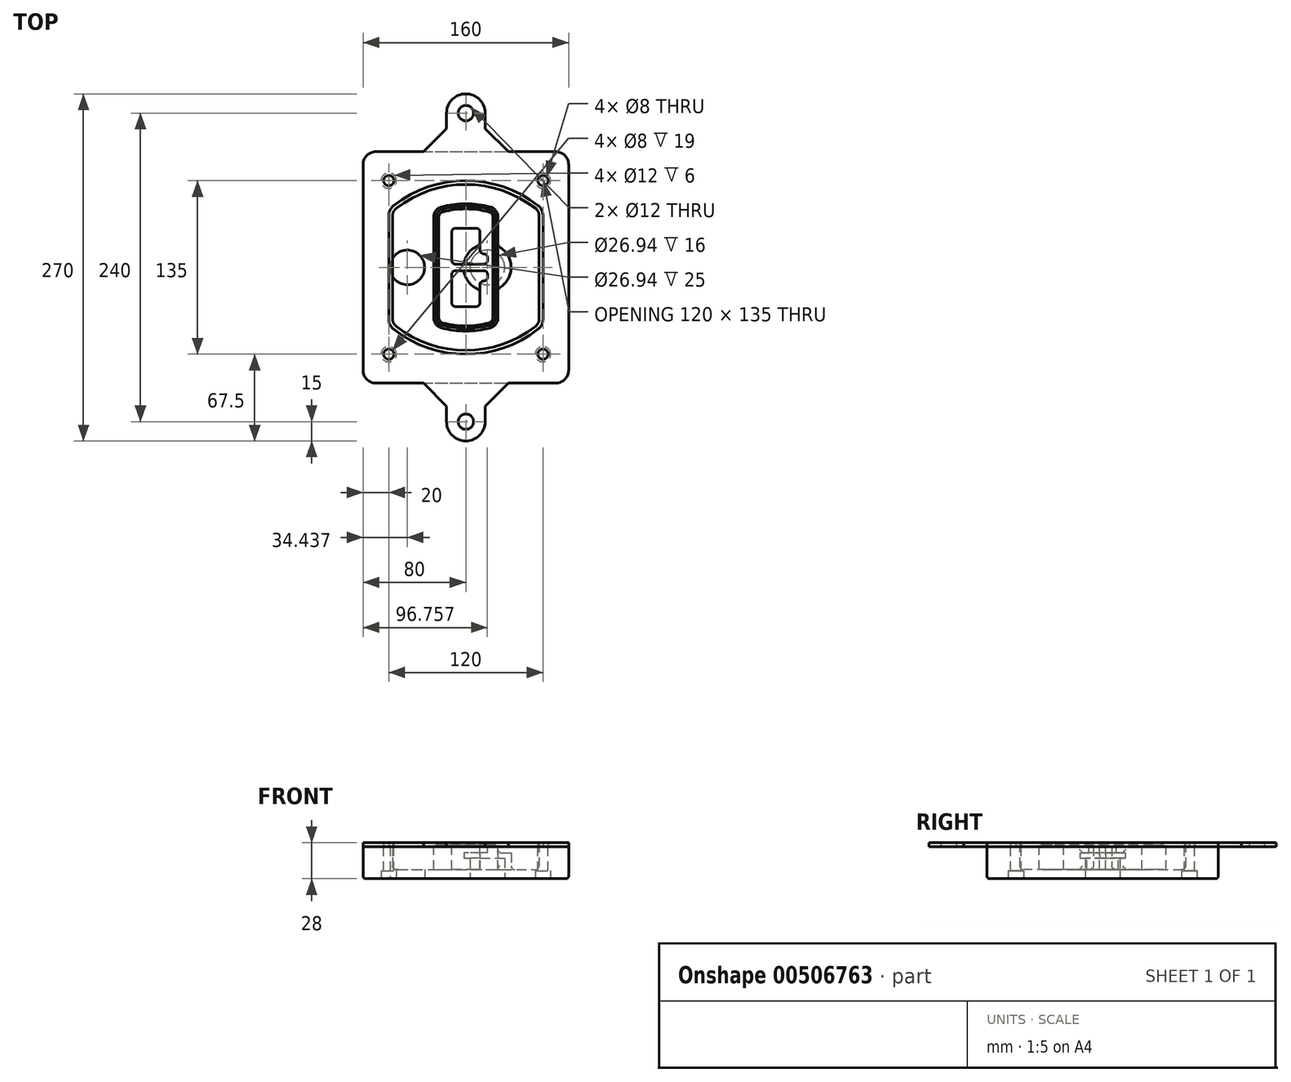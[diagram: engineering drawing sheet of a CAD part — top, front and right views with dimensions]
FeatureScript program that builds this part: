
annotation { "Feature Type Name" : "Feature", "Feature Type Description" : "" }
export const myFeature = defineFeature(function(context is Context, id is Id, definition is map)
    precondition{}
    {
        {
            var Q0;
            Q0=qCreatedBy(makeId("Top.planeOp"),FACE);
            var sketch = newSketch(context, id + "F0", { "sketchPlane" : qUnion([Q0])});
            skPoint(sketch, "E0.rect.middle", {"position": v(0, 0) * mm});
            skLineSegment(sketch, "E1.bottom", {"start": v(-70, -90) * mm, "end": v(70, -90) * mm});
            skLineSegment(sketch, "E1.top", {"start": v(-70, 90) * mm, "end": v(70, 90) * mm});
            skLineSegment(sketch, "E1.left", {"start": v(-80, -80) * mm, "end": v(-80, 80) * mm});
            skLineSegment(sketch, "E1.right", {"start": v(80, -80) * mm, "end": v(80, 80) * mm});
            skLineSegment(sketch, "E2", {"start": v(-80, 90) * mm, "end": v(80, -90) * mm, "construction": true});
            skLineSegment(sketch, "E3", {"start": v(80, 90) * mm, "end": v(-80, -90) * mm, "construction": true});
            skCircle(sketch, "E4", {"center": v(-60, 67.5) * mm, "radius": 4 * mm});
            skCircle(sketch, "E5", {"center": v(60, 67.5) * mm, "radius": 4 * mm});
            skCircle(sketch, "E6", {"center": v(60, -67.5) * mm, "radius": 4 * mm});
            skCircle(sketch, "E7", {"center": v(-60, -67.5) * mm, "radius": 4 * mm});
            skLineSegment(sketch, "E8", {"start": v(-60, 67.5) * mm, "end": v(60, 67.5) * mm, "construction": true});
            skLineSegment(sketch, "E9", {"start": v(60, 67.5) * mm, "end": v(60, -67.5) * mm, "construction": true});
            skLineSegment(sketch, "E10", {"start": v(60, -67.5) * mm, "end": v(-60, -67.5) * mm, "construction": true});
            skLineSegment(sketch, "E11", {"start": v(-60, -67.5) * mm, "end": v(-60, 67.5) * mm, "construction": true});
            skLineSegment(sketch, "E12", {"start": v(-60, 40.3) * mm, "end": v(-60, -40.3) * mm});
            skLineSegment(sketch, "E13", {"start": v(60, 40.3) * mm, "end": v(60, -40.3) * mm});
            skArc(sketch, "E14", {"start": v(56.15, 48.18) * mm, "mid": v(0, 67.5) * mm, "end": v(-56.15, 48.18) * mm});
            skArc(sketch, "E15", {"start": v(-56.15, -48.18) * mm, "mid": v(0, -67.5) * mm, "end": v(56.15, -48.18) * mm});
            skLineSegment(sketch, "E16", {"start": v(-60, 0) * mm, "end": v(60, 0) * mm, "construction": true});
            skPoint(sketch, "E17.visualSharp", {"position": v(-60, -45) * mm});
            skArc(sketch, "E17.filletArc", {"start": v(-60, -40.3) * mm, "mid": v(-58.99, -44.68) * mm, "end": v(-56.15, -48.18) * mm});
            skPoint(sketch, "E18.visualSharp", {"position": v(-60, 45) * mm});
            skArc(sketch, "E18.filletArc", {"start": v(-56.15, 48.18) * mm, "mid": v(-58.99, 44.68) * mm, "end": v(-60, 40.3) * mm});
            skPoint(sketch, "E19.visualSharp", {"position": v(60, 45) * mm});
            skArc(sketch, "E19.filletArc", {"start": v(60, 40.3) * mm, "mid": v(58.99, 44.68) * mm, "end": v(56.15, 48.18) * mm});
            skPoint(sketch, "E20.visualSharp", {"position": v(60, -45) * mm});
            skArc(sketch, "E20.filletArc", {"start": v(56.15, -48.18) * mm, "mid": v(58.99, -44.68) * mm, "end": v(60, -40.3) * mm});
            skPoint(sketch, "E21.visualSharp", {"position": v(-80, 90) * mm});
            skArc(sketch, "E21.filletArc", {"start": v(-70, 90) * mm, "mid": v(-77.07, 87.07) * mm, "end": v(-80, 80) * mm});
            skPoint(sketch, "E22.visualSharp", {"position": v(80, 90) * mm});
            skArc(sketch, "E22.filletArc", {"start": v(80, 80) * mm, "mid": v(77.07, 87.07) * mm, "end": v(70, 90) * mm});
            skPoint(sketch, "E23.visualSharp", {"position": v(80, -90) * mm});
            skArc(sketch, "E23.filletArc", {"start": v(70, -90) * mm, "mid": v(77.07, -87.07) * mm, "end": v(80, -80) * mm});
            skPoint(sketch, "E24.visualSharp", {"position": v(-80, -90) * mm});
            skArc(sketch, "E24.filletArc", {"start": v(-80, -80) * mm, "mid": v(-77.07, -87.07) * mm, "end": v(-70, -90) * mm});
            skArc(sketch, "E25.0", {"start": v(57, 40.3) * mm, "mid": v(56.3, 43.36) * mm, "end": v(54.3, 45.81) * mm});
            skLineSegment(sketch, "E25.1", {"start": v(57, 40.3) * mm, "end": v(57, -40.3) * mm});
            skArc(sketch, "E25.2", {"start": v(54.3, -45.81) * mm, "mid": v(56.3, -43.36) * mm, "end": v(57, -40.3) * mm});
            skArc(sketch, "E25.3", {"start": v(-54.3, -45.81) * mm, "mid": v(0, -64.5) * mm, "end": v(54.3, -45.81) * mm});
            skArc(sketch, "E25.4", {"start": v(-57, -40.3) * mm, "mid": v(-56.3, -43.36) * mm, "end": v(-54.3, -45.81) * mm});
            skArc(sketch, "E25.5", {"start": v(54.3, 45.81) * mm, "mid": v(0, 64.5) * mm, "end": v(-54.3, 45.81) * mm});
            skLineSegment(sketch, "E25.6", {"start": v(-57, 40.3) * mm, "end": v(-57, -40.3) * mm});
            skArc(sketch, "E25.7", {"start": v(-54.3, 45.81) * mm, "mid": v(-56.3, 43.36) * mm, "end": v(-57, 40.3) * mm});
            skArc(sketch, "E26.0", {"start": v(-58.62, 51.33) * mm, "mid": v(-62.58, 46.43) * mm, "end": v(-64, 40.3) * mm});
            skArc(sketch, "E26.1", {"start": v(58.62, 51.33) * mm, "mid": v(0, 71.5) * mm, "end": v(-58.62, 51.33) * mm});
            skArc(sketch, "E26.2", {"start": v(64, 40.3) * mm, "mid": v(62.58, 46.43) * mm, "end": v(58.62, 51.33) * mm});
            skLineSegment(sketch, "E26.3", {"start": v(64, 40.3) * mm, "end": v(64, -40.3) * mm});
            skArc(sketch, "E26.4", {"start": v(58.62, -51.33) * mm, "mid": v(62.58, -46.43) * mm, "end": v(64, -40.3) * mm});
            skLineSegment(sketch, "E26.5", {"start": v(-64, 40.3) * mm, "end": v(-64, -40.3) * mm});
            skArc(sketch, "E26.6", {"start": v(-58.62, -51.33) * mm, "mid": v(0, -71.5) * mm, "end": v(58.62, -51.33) * mm});
            skArc(sketch, "E26.7", {"start": v(-64, -40.3) * mm, "mid": v(-62.58, -46.43) * mm, "end": v(-58.62, -51.33) * mm});
            skSolve(sketch);
        }
        {
            var Q0;
            Q0=makeQuery(id+"F0.imprint","IMPRINT",FACE,{"disambiguationData":[TD([[makeQuery(id+"F0.imprint","IMPRINT",EDGE,{"derivedFrom":sQuery(id+"F0.wireOp",EDGE,"E1.bottom")}),1.0]])]});
            var Q1;
            Q1=makeQuery(id+"F0.imprint","IMPRINT",FACE,{"disambiguationData":[TD([[makeQuery(id+"F0.imprint","IMPRINT",EDGE,{"derivedFrom":sQuery(id+"F0.wireOp",EDGE,"E12")}),1.0]])]});
            var Q2;
            Q2=makeQuery(id+"F0.imprint","IMPRINT",FACE,{"disambiguationData":[TD([[makeQuery(id+"F0.imprint","IMPRINT",EDGE,{"derivedFrom":sQuery(id+"F0.wireOp",EDGE,"E25.0")}),1.0]])]});
            var Q3;
            Q3=makeQuery(id+"F0.imprint","IMPRINT",FACE,{"disambiguationData":[TD([[makeQuery(id+"F0.imprint","IMPRINT",EDGE,{"derivedFrom":sQuery(id+"F0.wireOp",EDGE,"E12")}),-1.0]])]});
            extrude(context, id + "F1", {"entities" : qUnion([Q0, Q1, Q2, Q3]), "oppositeDirection" : true, "depth" : 25 * mm});
        }
        {
            var Q0;
            Q0=makeQuery(id+"F0.imprint","IMPRINT",FACE,{"disambiguationData":[TD([[makeQuery(id+"F0.imprint","IMPRINT",EDGE,{"derivedFrom":sQuery(id+"F0.wireOp",EDGE,"E12")}),1.0]])]});
            extrude(context, id + "F2", {"entities" : qUnion([Q0]), "operationType" : NewBodyOperationType.ADD, "depth" : 3 * mm});
        }
        {
            var Q0;
            Q0=makeQuery(id+"F0.imprint","IMPRINT",FACE,{"disambiguationData":[TD([[makeQuery(id+"F0.imprint","IMPRINT",EDGE,{"derivedFrom":sQuery(id+"F0.wireOp",EDGE,"E25.0")}),1.0]])]});
            extrude(context, id + "F3", {"entities" : qUnion([Q0]), "operationType" : NewBodyOperationType.REMOVE, "oppositeDirection" : true, "depth" : 18 * mm});
        }
        {
            var Q0;
            Q0=makeQuery(id+"F2.opExtrude","CAP_FACE",FACE,{"disambiguationData":[OSD([sQuery(id+"F0.wireOp",EDGE,"E12"),sQuery(id+"F0.wireOp",EDGE,"E13"),sQuery(id+"F0.wireOp",EDGE,"E14"),sQuery(id+"F0.wireOp",EDGE,"E15"),sQuery(id+"F0.wireOp",EDGE,"E17.filletArc"),sQuery(id+"F0.wireOp",EDGE,"E18.filletArc"),sQuery(id+"F0.wireOp",EDGE,"E19.filletArc"),sQuery(id+"F0.wireOp",EDGE,"E20.filletArc"),sQuery(id+"F0.wireOp",EDGE,"E25.0"),sQuery(id+"F0.wireOp",EDGE,"E25.1"),sQuery(id+"F0.wireOp",EDGE,"E25.2"),sQuery(id+"F0.wireOp",EDGE,"E25.3"),sQuery(id+"F0.wireOp",EDGE,"E25.4"),sQuery(id+"F0.wireOp",EDGE,"E25.5"),sQuery(id+"F0.wireOp",EDGE,"E25.6"),sQuery(id+"F0.wireOp",EDGE,"E25.7")])],"isStart":false});
            var sketch = newSketch(context, id + "F4", { "sketchPlane" : qUnion([Q0])});
            skArc(sketch, "E27.0", {"start": v(-19.08, -46.97) * mm, "mid": v(0, -49.5) * mm, "end": v(19.08, -46.97) * mm});
            skArc(sketch, "E28.0", {"start": v(19.08, 46.97) * mm, "mid": v(0, 49.5) * mm, "end": v(-19.08, 46.97) * mm});
            skLineSegment(sketch, "E29", {"start": v(-25, 39.25) * mm, "end": v(-25, -39.25) * mm});
            skLineSegment(sketch, "E30", {"start": v(25, 39.25) * mm, "end": v(25, -39.25) * mm});
            skLineSegment(sketch, "E31", {"start": v(-25, 45.1) * mm, "end": v(25, 45.1) * mm, "construction": true});
            skLineSegment(sketch, "E32", {"start": v(-25, -45.1) * mm, "end": v(25, -45.1) * mm, "construction": true});
            skPoint(sketch, "E33.visualSharp", {"position": v(-25, 45.1) * mm});
            skArc(sketch, "E33.filletArc", {"start": v(-19.08, 46.97) * mm, "mid": v(-23.35, 44.11) * mm, "end": v(-25, 39.25) * mm});
            skPoint(sketch, "E34.visualSharp", {"position": v(25, 45.1) * mm});
            skArc(sketch, "E34.filletArc", {"start": v(25, 39.25) * mm, "mid": v(23.35, 44.11) * mm, "end": v(19.08, 46.97) * mm});
            skPoint(sketch, "E35.visualSharp", {"position": v(25, -45.1) * mm});
            skArc(sketch, "E35.filletArc", {"start": v(19.08, -46.97) * mm, "mid": v(23.35, -44.11) * mm, "end": v(25, -39.25) * mm});
            skPoint(sketch, "E36.visualSharp", {"position": v(-25, -45.1) * mm});
            skArc(sketch, "E36.filletArc", {"start": v(-25, -39.25) * mm, "mid": v(-23.35, -44.11) * mm, "end": v(-19.08, -46.97) * mm});
            skArc(sketch, "E37.0", {"start": v(54.3, 45.81) * mm, "mid": v(0, 64.5) * mm, "end": v(-54.3, 45.81) * mm});
            skArc(sketch, "E37.1", {"start": v(-54.3, 45.81) * mm, "mid": v(-56.3, 43.36) * mm, "end": v(-57, 40.3) * mm});
            skLineSegment(sketch, "E37.2", {"start": v(-57, 40.3) * mm, "end": v(-57, -40.3) * mm});
            skArc(sketch, "E37.3", {"start": v(-57, -40.3) * mm, "mid": v(-56.3, -43.36) * mm, "end": v(-54.3, -45.81) * mm});
            skArc(sketch, "E37.4", {"start": v(-54.3, -45.81) * mm, "mid": v(0, -64.5) * mm, "end": v(54.3, -45.81) * mm});
            skArc(sketch, "E37.5", {"start": v(54.3, -45.81) * mm, "mid": v(56.3, -43.36) * mm, "end": v(57, -40.3) * mm});
            skLineSegment(sketch, "E37.6", {"start": v(57, 40.3) * mm, "end": v(57, -40.3) * mm});
            skArc(sketch, "E37.7", {"start": v(57, 40.3) * mm, "mid": v(56.3, 43.36) * mm, "end": v(54.3, 45.81) * mm});
            skLineSegment(sketch, "E38.0", {"start": v(23, 39.25) * mm, "end": v(23, -39.25) * mm});
            skArc(sketch, "E38.1", {"start": v(18.56, -45.04) * mm, "mid": v(21.76, -42.9) * mm, "end": v(23, -39.25) * mm});
            skArc(sketch, "E38.2", {"start": v(-18.56, -45.04) * mm, "mid": v(0, -47.5) * mm, "end": v(18.56, -45.04) * mm});
            skArc(sketch, "E38.3", {"start": v(-23, -39.25) * mm, "mid": v(-21.76, -42.9) * mm, "end": v(-18.56, -45.04) * mm});
            skLineSegment(sketch, "E38.4", {"start": v(-23, 39.25) * mm, "end": v(-23, -39.25) * mm});
            skArc(sketch, "E38.5", {"start": v(23, 39.25) * mm, "mid": v(21.76, 42.9) * mm, "end": v(18.56, 45.04) * mm});
            skArc(sketch, "E38.6", {"start": v(-18.56, 45.04) * mm, "mid": v(-21.76, 42.9) * mm, "end": v(-23, 39.25) * mm});
            skArc(sketch, "E38.7", {"start": v(18.56, 45.04) * mm, "mid": v(0, 47.5) * mm, "end": v(-18.56, 45.04) * mm});
            skArc(sketch, "E39.0", {"start": v(21, 39.25) * mm, "mid": v(20.18, 41.68) * mm, "end": v(18.04, 43.1) * mm});
            skLineSegment(sketch, "E39.1", {"start": v(21, 39.25) * mm, "end": v(21, -39.25) * mm});
            skArc(sketch, "E39.2", {"start": v(18.04, -43.1) * mm, "mid": v(20.18, -41.68) * mm, "end": v(21, -39.25) * mm});
            skArc(sketch, "E39.3", {"start": v(-18.04, -43.1) * mm, "mid": v(0, -45.5) * mm, "end": v(18.04, -43.1) * mm});
            skArc(sketch, "E39.4", {"start": v(-21, -39.25) * mm, "mid": v(-20.18, -41.68) * mm, "end": v(-18.04, -43.1) * mm});
            skArc(sketch, "E39.5", {"start": v(18.04, 43.1) * mm, "mid": v(0, 45.5) * mm, "end": v(-18.04, 43.1) * mm});
            skLineSegment(sketch, "E39.6", {"start": v(-21, 39.25) * mm, "end": v(-21, -39.25) * mm});
            skArc(sketch, "E39.7", {"start": v(-18.04, 43.1) * mm, "mid": v(-20.18, 41.68) * mm, "end": v(-21, 39.25) * mm});
            skLineSegment(sketch, "E40", {"start": v(-25, 0) * mm, "end": v(25, 0) * mm, "construction": true});
            skLineSegment(sketch, "E41", {"start": v(-11, 5.5) * mm, "end": v(-11, 27.5) * mm});
            skLineSegment(sketch, "E42", {"start": v(-8, 30.5) * mm, "end": v(8, 30.5) * mm});
            skLineSegment(sketch, "E43", {"start": v(11, 27.5) * mm, "end": v(11, 13.5) * mm});
            skLineSegment(sketch, "E44", {"start": v(14, 10.5) * mm, "end": v(14, 10.5) * mm});
            skLineSegment(sketch, "E45", {"start": v(17, 7.5) * mm, "end": v(17, 5.5) * mm});
            skLineSegment(sketch, "E46", {"start": v(14, 2.5) * mm, "end": v(-8, 2.5) * mm});
            skPoint(sketch, "E47.visualSharp", {"position": v(-11, 30.5) * mm});
            skArc(sketch, "E47.filletArc", {"start": v(-8, 30.5) * mm, "mid": v(-10.12, 29.62) * mm, "end": v(-11, 27.5) * mm});
            skPoint(sketch, "E48.visualSharp", {"position": v(11, 30.5) * mm});
            skArc(sketch, "E48.filletArc", {"start": v(11, 27.5) * mm, "mid": v(10.12, 29.62) * mm, "end": v(8, 30.5) * mm});
            skPoint(sketch, "E49.visualSharp", {"position": v(11, 10.5) * mm});
            skArc(sketch, "E49.filletArc", {"start": v(11, 13.5) * mm, "mid": v(11.88, 11.38) * mm, "end": v(14, 10.5) * mm});
            skPoint(sketch, "E50.visualSharp", {"position": v(17, 10.5) * mm});
            skArc(sketch, "E50.filletArc", {"start": v(17, 7.5) * mm, "mid": v(16.12, 9.62) * mm, "end": v(14, 10.5) * mm});
            skPoint(sketch, "E51.visualSharp", {"position": v(17, 2.5) * mm});
            skArc(sketch, "E51.filletArc", {"start": v(14, 2.5) * mm, "mid": v(16.12, 3.38) * mm, "end": v(17, 5.5) * mm});
            skPoint(sketch, "E52.visualSharp", {"position": v(-11, 2.5) * mm});
            skArc(sketch, "E52.filletArc", {"start": v(-11, 5.5) * mm, "mid": v(-10.12, 3.38) * mm, "end": v(-8, 2.5) * mm});
            skLineSegment(sketch, "E53.0.MirrorCS", {"start": v(14, -2.5) * mm, "end": v(-8, -2.5) * mm});
            skArc(sketch, "E54.0.MirrorCS", {"start": v(-11, -5.5) * mm, "mid": v(-10.12, -3.38) * mm, "end": v(-8, -2.5) * mm});
            skLineSegment(sketch, "E55.0.MirrorCS", {"start": v(-11, -5.5) * mm, "end": v(-11, -27.5) * mm});
            skArc(sketch, "E56.0.MirrorCS", {"start": v(-8, -30.5) * mm, "mid": v(-10.12, -29.62) * mm, "end": v(-11, -27.5) * mm});
            skLineSegment(sketch, "E57.0.MirrorCS", {"start": v(-8, -30.5) * mm, "end": v(8, -30.5) * mm});
            skArc(sketch, "E58.0.MirrorCS", {"start": v(11, -27.5) * mm, "mid": v(10.12, -29.62) * mm, "end": v(8, -30.5) * mm});
            skLineSegment(sketch, "E59.0.MirrorCS", {"start": v(11, -27.5) * mm, "end": v(11, -13.5) * mm});
            skArc(sketch, "E60.0.MirrorCS", {"start": v(11, -13.5) * mm, "mid": v(11.88, -11.38) * mm, "end": v(14, -10.5) * mm});
            skArc(sketch, "E61.0.MirrorCS", {"start": v(17, -7.5) * mm, "mid": v(16.12, -9.62) * mm, "end": v(14, -10.5) * mm});
            skLineSegment(sketch, "E62.0.MirrorCS", {"start": v(17, -7.5) * mm, "end": v(17, -5.5) * mm});
            skArc(sketch, "E63.0.MirrorCS", {"start": v(14, -2.5) * mm, "mid": v(16.12, -3.38) * mm, "end": v(17, -5.5) * mm});
            skSolve(sketch);
        }
        {
            var Q0;
            Q0=makeQuery(id+"F4.imprint","IMPRINT",FACE,{"disambiguationData":[TD([[makeQuery(id+"F4.imprint","IMPRINT",EDGE,{"derivedFrom":sQuery(id+"F4.wireOp",EDGE,"E27.0")}),1.0]])]});
            var Q1;
            Q1=makeQuery(id+"F4.imprint","IMPRINT",FACE,{"disambiguationData":[TD([[makeQuery(id+"F4.imprint","IMPRINT",EDGE,{"derivedFrom":sQuery(id+"F4.wireOp",EDGE,"E38.0")}),-1.0]])]});
            var Q2;
            Q2=makeQuery(id+"F4.imprint","IMPRINT",FACE,{"disambiguationData":[TD([[makeQuery(id+"F4.imprint","IMPRINT",EDGE,{"derivedFrom":sQuery(id+"F4.wireOp",EDGE,"E39.0")}),1.0]])]});
            extrude(context, id + "F5", {"entities" : qUnion([Q0, Q1, Q2]), "operationType" : NewBodyOperationType.ADD, "endBound" : BoundingType.UP_TO_NEXT, "oppositeDirection" : true, "depth" : 25 * mm});
        }
        {
            var Q0;
            Q0=makeQuery(id+"F4.imprint","IMPRINT",FACE,{"disambiguationData":[TD([[makeQuery(id+"F4.imprint","IMPRINT",EDGE,{"derivedFrom":sQuery(id+"F4.wireOp",EDGE,"E38.0")}),-1.0]])]});
            extrude(context, id + "F6", {"entities" : qUnion([Q0]), "operationType" : NewBodyOperationType.REMOVE, "oppositeDirection" : true, "depth" : 2 * mm});
        }
        {
            var Q0;
            Q0=makeQuery(id+"F1.opExtrude","CAP_FACE",FACE,{"disambiguationData":[OSD([sQuery(id+"F0.wireOp",EDGE,"E1.bottom"),sQuery(id+"F0.wireOp",EDGE,"E1.top"),sQuery(id+"F0.wireOp",EDGE,"E1.left"),sQuery(id+"F0.wireOp",EDGE,"E1.right"),sQuery(id+"F0.wireOp",EDGE,"E4"),sQuery(id+"F0.wireOp",EDGE,"E5"),sQuery(id+"F0.wireOp",EDGE,"E6"),sQuery(id+"F0.wireOp",EDGE,"E7"),sQuery(id+"F0.wireOp",EDGE,"E21.filletArc"),sQuery(id+"F0.wireOp",EDGE,"E22.filletArc"),sQuery(id+"F0.wireOp",EDGE,"E23.filletArc"),sQuery(id+"F0.wireOp",EDGE,"E24.filletArc")])],"isStart":false});
            var sketch = newSketch(context, id + "F7", { "sketchPlane" : qUnion([Q0])});
            skCircle(sketch, "E64", {"center": v(16.76, 0) * mm, "radius": 13.47 * mm});
            skCircle(sketch, "E65", {"center": v(-45.56, 0) * mm, "radius": 13.47 * mm});
            skLineSegment(sketch, "E66", {"start": v(80, 0) * mm, "end": v(-80, 0) * mm});
            skCircle(sketch, "E67", {"center": v(16.76, 0) * mm, "radius": 18.47 * mm});
            skCircle(sketch, "E68", {"center": v(60, -67.5) * mm, "radius": 6 * mm});
            skCircle(sketch, "E69", {"center": v(-60, -67.5) * mm, "radius": 6 * mm});
            skCircle(sketch, "E70", {"center": v(-60, 67.5) * mm, "radius": 6 * mm});
            skCircle(sketch, "E71", {"center": v(60, 67.5) * mm, "radius": 6 * mm});
            skSolve(sketch);
        }
        {
            var Q0;
            {var subQ1=sQuery(id+"F7.wireOp",EDGE,"E66");var subQ4=sQuery(id+"F7.wireOp",EDGE,"E64");var subQ6=makeQuery(id+"F7.imprint","INTERSECT",VERTEX,{"disambiguationData":[OD(0.0)],"derivedFrom":[subQ4,subQ1]});Q0=makeQuery(id+"F7.imprint","IMPRINT",FACE,{"disambiguationData":[TD([[makeQuery(id+"F7.imprint","IMPRINT",EDGE,{"disambiguationData":[TD([[subQ6,-1.0]])],"derivedFrom":subQ4}),-1.0]])]});}
            var Q1;
            {var subQ0=sQuery(id+"F7.wireOp",EDGE,"E66");var subQ1=sQuery(id+"F7.wireOp",EDGE,"E64");var subQ3=makeQuery(id+"F7.imprint","INTERSECT",VERTEX,{"disambiguationData":[OD(0.0)],"derivedFrom":[subQ1,subQ0]});Q1=makeQuery(id+"F7.imprint","IMPRINT",FACE,{"disambiguationData":[TD([[makeQuery(id+"F7.imprint","IMPRINT",EDGE,{"disambiguationData":[TD([[subQ3,-1.0]])],"derivedFrom":subQ1}),1.0]])]});}
            var Q2;
            {var subQ0=sQuery(id+"F7.wireOp",EDGE,"E66");var subQ1=sQuery(id+"F7.wireOp",EDGE,"E64");var subQ3=makeQuery(id+"F7.imprint","INTERSECT",VERTEX,{"disambiguationData":[OD(0.0)],"derivedFrom":[subQ1,subQ0]});Q2=makeQuery(id+"F7.imprint","IMPRINT",FACE,{"disambiguationData":[TD([[makeQuery(id+"F7.imprint","IMPRINT",EDGE,{"disambiguationData":[TD([[subQ3,1.0]])],"derivedFrom":subQ1}),1.0]])]});}
            var Q3;
            {var subQ1=sQuery(id+"F7.wireOp",EDGE,"E66");var subQ4=sQuery(id+"F7.wireOp",EDGE,"E64");var subQ6=makeQuery(id+"F7.imprint","INTERSECT",VERTEX,{"disambiguationData":[OD(0.0)],"derivedFrom":[subQ4,subQ1]});Q3=makeQuery(id+"F7.imprint","IMPRINT",FACE,{"disambiguationData":[TD([[makeQuery(id+"F7.imprint","IMPRINT",EDGE,{"disambiguationData":[TD([[subQ6,1.0]])],"derivedFrom":subQ4}),-1.0]])]});}
            extrude(context, id + "F8", {"entities" : qUnion([Q0, Q1, Q2, Q3]), "operationType" : NewBodyOperationType.ADD, "oppositeDirection" : true, "depth" : 20 * mm});
        }
        {
            var Q0;
            {var subQ0=sQuery(id+"F7.wireOp",EDGE,"E66");var subQ1=sQuery(id+"F7.wireOp",EDGE,"E64");var subQ3=makeQuery(id+"F7.imprint","INTERSECT",VERTEX,{"disambiguationData":[OD(0.0)],"derivedFrom":[subQ1,subQ0]});Q0=makeQuery(id+"F7.imprint","IMPRINT",FACE,{"disambiguationData":[TD([[makeQuery(id+"F7.imprint","IMPRINT",EDGE,{"disambiguationData":[TD([[subQ3,-1.0]])],"derivedFrom":subQ1}),1.0]])]});}
            var Q1;
            {var subQ0=sQuery(id+"F7.wireOp",EDGE,"E66");var subQ1=sQuery(id+"F7.wireOp",EDGE,"E64");var subQ3=makeQuery(id+"F7.imprint","INTERSECT",VERTEX,{"disambiguationData":[OD(0.0)],"derivedFrom":[subQ1,subQ0]});Q1=makeQuery(id+"F7.imprint","IMPRINT",FACE,{"disambiguationData":[TD([[makeQuery(id+"F7.imprint","IMPRINT",EDGE,{"disambiguationData":[TD([[subQ3,1.0]])],"derivedFrom":subQ1}),1.0]])]});}
            extrude(context, id + "F9", {"entities" : qUnion([Q0, Q1]), "operationType" : NewBodyOperationType.REMOVE, "oppositeDirection" : true, "depth" : 16 * mm});
        }
        {
            var Q0;
            {var subQ0=sQuery(id+"F7.wireOp",EDGE,"E66");var subQ1=sQuery(id+"F7.wireOp",EDGE,"E65");var subQ3=makeQuery(id+"F7.imprint","INTERSECT",VERTEX,{"disambiguationData":[OD(0.0)],"derivedFrom":[subQ1,subQ0]});Q0=makeQuery(id+"F7.imprint","IMPRINT",FACE,{"disambiguationData":[TD([[makeQuery(id+"F7.imprint","IMPRINT",EDGE,{"disambiguationData":[TD([[subQ3,-1.0]])],"derivedFrom":subQ1}),1.0]])]});}
            var Q1;
            {var subQ0=sQuery(id+"F7.wireOp",EDGE,"E66");var subQ1=sQuery(id+"F7.wireOp",EDGE,"E65");var subQ3=makeQuery(id+"F7.imprint","INTERSECT",VERTEX,{"disambiguationData":[OD(0.0)],"derivedFrom":[subQ1,subQ0]});Q1=makeQuery(id+"F7.imprint","IMPRINT",FACE,{"disambiguationData":[TD([[makeQuery(id+"F7.imprint","IMPRINT",EDGE,{"disambiguationData":[TD([[subQ3,1.0]])],"derivedFrom":subQ1}),1.0]])]});}
            extrude(context, id + "F10", {"entities" : qUnion([Q0, Q1]), "operationType" : NewBodyOperationType.REMOVE, "oppositeDirection" : true, "depth" : 25 * mm});
        }
        {
            var Q0;
            Q0=makeQuery(id+"F7.imprint","IMPRINT",FACE,{"disambiguationData":[TD([[makeQuery(id+"F7.imprint","IMPRINT",EDGE,{"derivedFrom":sQuery(id+"F7.wireOp",EDGE,"E68")}),1.0]])]});
            var Q1;
            Q1=makeQuery(id+"F7.imprint","IMPRINT",FACE,{"disambiguationData":[TD([[makeQuery(id+"F7.imprint","IMPRINT",EDGE,{"derivedFrom":makeQuery(id+"F1.opExtrude","CAP_EDGE",EDGE,{"disambiguationData":[OSD([sQuery(id+"F0.wireOp",EDGE,"E5")])],"isStart":false})}),-1.0]])]});
            var Q2;
            Q2=makeQuery(id+"F7.imprint","IMPRINT",FACE,{"disambiguationData":[TD([[makeQuery(id+"F7.imprint","IMPRINT",EDGE,{"derivedFrom":sQuery(id+"F7.wireOp",EDGE,"E69")}),1.0]])]});
            var Q3;
            Q3=makeQuery(id+"F7.imprint","IMPRINT",FACE,{"disambiguationData":[TD([[makeQuery(id+"F7.imprint","IMPRINT",EDGE,{"derivedFrom":makeQuery(id+"F1.opExtrude","CAP_EDGE",EDGE,{"disambiguationData":[OSD([sQuery(id+"F0.wireOp",EDGE,"E4")])],"isStart":false})}),-1.0]])]});
            var Q4;
            Q4=makeQuery(id+"F7.imprint","IMPRINT",FACE,{"disambiguationData":[TD([[makeQuery(id+"F7.imprint","IMPRINT",EDGE,{"derivedFrom":sQuery(id+"F7.wireOp",EDGE,"E70")}),1.0]])]});
            var Q5;
            Q5=makeQuery(id+"F7.imprint","IMPRINT",FACE,{"disambiguationData":[TD([[makeQuery(id+"F7.imprint","IMPRINT",EDGE,{"derivedFrom":makeQuery(id+"F1.opExtrude","CAP_EDGE",EDGE,{"disambiguationData":[OSD([sQuery(id+"F0.wireOp",EDGE,"E7")])],"isStart":false})}),-1.0]])]});
            var Q6;
            Q6=makeQuery(id+"F7.imprint","IMPRINT",FACE,{"disambiguationData":[TD([[makeQuery(id+"F7.imprint","IMPRINT",EDGE,{"derivedFrom":sQuery(id+"F7.wireOp",EDGE,"E71")}),1.0]])]});
            var Q7;
            Q7=makeQuery(id+"F7.imprint","IMPRINT",FACE,{"disambiguationData":[TD([[makeQuery(id+"F7.imprint","IMPRINT",EDGE,{"derivedFrom":makeQuery(id+"F1.opExtrude","CAP_EDGE",EDGE,{"disambiguationData":[OSD([sQuery(id+"F0.wireOp",EDGE,"E6")])],"isStart":false})}),-1.0]])]});
            extrude(context, id + "F11", {"entities" : qUnion([Q0, Q1, Q2, Q3, Q4, Q5, Q6, Q7]), "operationType" : NewBodyOperationType.REMOVE, "oppositeDirection" : true, "depth" : 6 * mm});
        }
        {
            var Q0;
            Q0=makeQuery(id+"F9.boolean.opBoolean","COPY",FACE,{"derivedFrom":makeQuery(id+"F9.opExtrude","CAP_FACE",FACE,{"disambiguationData":[OSD([sQuery(id+"F7.wireOp",EDGE,"E64")])],"isStart":false})});
            var sketch = newSketch(context, id + "F12", { "sketchPlane" : qUnion([Q0])});
            skArc(sketch, "E72.0", {"start": v(11, 17.55) * mm, "mid": v(2.57, 11.82) * mm, "end": v(-1.54, 2.5) * mm});
            skArc(sketch, "E72.1", {"start": v(-1.54, -2.5) * mm, "mid": v(2.57, -11.82) * mm, "end": v(11, -17.55) * mm});
            skLineSegment(sketch, "E73", {"start": v(-1.54, -2.5) * mm, "end": v(14, -2.5) * mm});
            skLineSegment(sketch, "E74.0", {"start": v(14, 2.5) * mm, "end": v(-1.54, 2.5) * mm});
            skArc(sketch, "E74.1", {"start": v(14, 2.5) * mm, "mid": v(16.12, 3.38) * mm, "end": v(17, 5.5) * mm});
            skLineSegment(sketch, "E74.2", {"start": v(17, 7.5) * mm, "end": v(17, 5.5) * mm});
            skArc(sketch, "E74.3", {"start": v(17, 7.5) * mm, "mid": v(16.12, 9.62) * mm, "end": v(14, 10.5) * mm});
            skArc(sketch, "E74.4", {"start": v(11, 13.5) * mm, "mid": v(11.88, 11.38) * mm, "end": v(14, 10.5) * mm});
            skLineSegment(sketch, "E74.5", {"start": v(11, 17.55) * mm, "end": v(11, 13.5) * mm});
            skLineSegment(sketch, "E74.7", {"start": v(14, -2.5) * mm, "end": v(-1.54, -2.5) * mm});
            skArc(sketch, "E74.8", {"start": v(14, -2.5) * mm, "mid": v(16.12, -3.38) * mm, "end": v(17, -5.5) * mm});
            skLineSegment(sketch, "E74.9", {"start": v(17, -7.5) * mm, "end": v(17, -5.5) * mm});
            skArc(sketch, "E74.10", {"start": v(17, -7.5) * mm, "mid": v(16.12, -9.62) * mm, "end": v(14, -10.5) * mm});
            skArc(sketch, "E74.11", {"start": v(11, -13.5) * mm, "mid": v(11.88, -11.38) * mm, "end": v(14, -10.5) * mm});
            skLineSegment(sketch, "E74.12", {"start": v(11, -17.55) * mm, "end": v(11, -13.5) * mm});
            skPoint(sketch, "E75.orphan", {"position": v(11, -27.5) * mm});
            skPoint(sketch, "E76.orphan", {"position": v(-8, -2.5) * mm});
            skPoint(sketch, "E77.orphan", {"position": v(-8, 2.5) * mm});
            skPoint(sketch, "E78.orphan", {"position": v(11, 27.5) * mm});
            skSolve(sketch);
        }
        {
            var Q0;
            {var subQ7=sQuery(id+"F12.wireOp",EDGE,"E72.0");var subQ14=sQuery(id+"F12.wireOp",EDGE,"E72.1");var subQ16=sQuery(id+"F12.wireOp",EDGE,"E74.1");var subQ18=sQuery(id+"F12.wireOp",EDGE,"E74.8");Q0=qUnion([makeQuery(id+"F12.imprint","IMPRINT",FACE,{"disambiguationData":[TD([[makeQuery(id+"F12.imprint","IMPRINT",EDGE,{"derivedFrom":subQ7}),1.0]])]}),makeQuery(id+"F12.imprint","IMPRINT",FACE,{"disambiguationData":[TD([[makeQuery(id+"F12.imprint","IMPRINT",EDGE,{"derivedFrom":subQ14}),1.0]])]}),makeQuery(id+"F12.imprint","IMPRINT",FACE,{"disambiguationData":[TD([[makeQuery(id+"F12.imprint","IMPRINT",EDGE,{"derivedFrom":subQ16}),1.0]])]}),makeQuery(id+"F12.imprint","IMPRINT",FACE,{"disambiguationData":[TD([[makeQuery(id+"F12.imprint","IMPRINT",EDGE,{"derivedFrom":subQ18}),-1.0]])]})]);}
            var Q1;
            Q1=makeQuery(id+"F5.boolean.opBoolean","SPLIT",FACE,{"disambiguationData":[TD([makeQuery(id+"F5.opExtrude","SWEPT_FACE",FACE,{"disambiguationData":[OSD([sQuery(id+"F4.wireOp",EDGE,"E41")])]})])],"derivedFrom":makeQuery(id+"F3.boolean.opBoolean","COPY",FACE,{"derivedFrom":makeQuery(id+"F3.opExtrude","CAP_FACE",FACE,{"disambiguationData":[OSD([sQuery(id+"F0.wireOp",EDGE,"E25.0"),sQuery(id+"F0.wireOp",EDGE,"E25.1"),sQuery(id+"F0.wireOp",EDGE,"E25.2"),sQuery(id+"F0.wireOp",EDGE,"E25.3"),sQuery(id+"F0.wireOp",EDGE,"E25.4"),sQuery(id+"F0.wireOp",EDGE,"E25.5"),sQuery(id+"F0.wireOp",EDGE,"E25.6"),sQuery(id+"F0.wireOp",EDGE,"E25.7")])],"isStart":false})})});
            extrude(context, id + "F13", {"entities" : qUnion([Q0]), "operationType" : NewBodyOperationType.REMOVE, "endBound" : BoundingType.UP_TO_SURFACE, "endBoundEntityFace" : qUnion([Q1]), "depth" : 25 * mm});
        }
        {
            var Q0;
            Q0=makeQuery(id+"F3.boolean.opBoolean","COPY",EDGE,{"derivedFrom":makeQuery(id+"F3.opExtrude","CAP_EDGE",EDGE,{"disambiguationData":[OSD([sQuery(id+"F0.wireOp",EDGE,"E25.6")])],"isStart":false})});
            var Q1;
            Q1=makeQuery(id+"F8.boolean.opBoolean","INTERSECT",EDGE,{"derivedFrom":[makeQuery(id+"F5.opExtrude","SWEPT_FACE",FACE,{"disambiguationData":[OSD([sQuery(id+"F4.wireOp",EDGE,"E30")])]}),makeQuery(id+"F8.opExtrude","CAP_FACE",FACE,{"disambiguationData":[OSD([sQuery(id+"F7.wireOp",EDGE,"E67")])],"isStart":false})]});
            var Q2;
            Q2=makeQuery(id+"F8.boolean.opBoolean","INTERSECT",EDGE,{"disambiguationData":[OD(1.0)],"derivedFrom":[makeQuery(id+"F5.opExtrude","SWEPT_FACE",FACE,{"disambiguationData":[OSD([sQuery(id+"F4.wireOp",EDGE,"E30")])]}),makeQuery(id+"F8.opExtrude","SWEPT_FACE",FACE,{"disambiguationData":[OSD([sQuery(id+"F7.wireOp",EDGE,"E67")])]})]});
            var Q3;
            {var subQ0=makeQuery(id+"F3.boolean.opBoolean","COPY",FACE,{"derivedFrom":makeQuery(id+"F3.opExtrude","CAP_FACE",FACE,{"disambiguationData":[OSD([sQuery(id+"F0.wireOp",EDGE,"E25.0"),sQuery(id+"F0.wireOp",EDGE,"E25.1"),sQuery(id+"F0.wireOp",EDGE,"E25.2"),sQuery(id+"F0.wireOp",EDGE,"E25.3"),sQuery(id+"F0.wireOp",EDGE,"E25.4"),sQuery(id+"F0.wireOp",EDGE,"E25.5"),sQuery(id+"F0.wireOp",EDGE,"E25.6"),sQuery(id+"F0.wireOp",EDGE,"E25.7")])],"isStart":false})});var subQ1=sQuery(id+"F4.wireOp",EDGE,"E30");Q3=makeQuery(id+"F8.boolean.opBoolean","SPLIT",EDGE,{"disambiguationData":[TD([makeQuery(id+"F5.opExtrude","SWEPT_FACE",FACE,{"disambiguationData":[OSD([sQuery(id+"F4.wireOp",EDGE,"E35.filletArc")])]})])],"derivedFrom":makeQuery(id+"F5.opExtrude","TWEAK_EDGE",EDGE,{"derivedFrom":[subQ0,makeQuery(id+"F4.imprint","IMPRINT",EDGE,{"derivedFrom":subQ1})]})});}
            var Q4;
            {var subQ0=sQuery(id+"F0.wireOp",EDGE,"E25.0");var subQ1=sQuery(id+"F0.wireOp",EDGE,"E25.1");var subQ2=sQuery(id+"F0.wireOp",EDGE,"E25.2");var subQ3=sQuery(id+"F0.wireOp",EDGE,"E25.3");var subQ4=sQuery(id+"F0.wireOp",EDGE,"E25.4");var subQ5=sQuery(id+"F0.wireOp",EDGE,"E25.5");var subQ6=sQuery(id+"F0.wireOp",EDGE,"E25.6");var subQ7=sQuery(id+"F0.wireOp",EDGE,"E25.7");Q4=makeQuery(id+"F8.boolean.opBoolean","INTERSECT",EDGE,{"derivedFrom":[makeQuery(id+"F5.boolean.opBoolean","SPLIT",FACE,{"disambiguationData":[TD([makeQuery(id+"F2.opExtrude","SWEPT_FACE",FACE,{"disambiguationData":[OSD([subQ0])]})])],"derivedFrom":makeQuery(id+"F3.boolean.opBoolean","COPY",FACE,{"derivedFrom":makeQuery(id+"F3.opExtrude","CAP_FACE",FACE,{"disambiguationData":[OSD([subQ0,subQ1,subQ2,subQ3,subQ4,subQ5,subQ6,subQ7])],"isStart":false})})}),makeQuery(id+"F8.opExtrude","SWEPT_FACE",FACE,{"disambiguationData":[OSD([sQuery(id+"F7.wireOp",EDGE,"E67")])]})]});}
            var Q5;
            Q5=makeQuery(id+"F8.boolean.opBoolean","INTERSECT",EDGE,{"disambiguationData":[OD(0.0)],"derivedFrom":[makeQuery(id+"F5.opExtrude","SWEPT_FACE",FACE,{"disambiguationData":[OSD([sQuery(id+"F4.wireOp",EDGE,"E30")])]}),makeQuery(id+"F8.opExtrude","SWEPT_FACE",FACE,{"disambiguationData":[OSD([sQuery(id+"F7.wireOp",EDGE,"E67")])]})]});
            fillet(context, id + "F14", {"entities" : qUnion([Q0, Q1, Q2, Q3, Q4, Q5]), "radius" : 3 * mm, "tangentPropagation" : true, "allowEdgeOverflow" : false});
        }
        {
            var Q0;
            Q0=makeQuery(id+"F1.opExtrude","CAP_EDGE",EDGE,{"disambiguationData":[OSD([sQuery(id+"F0.wireOp",EDGE,"E1.bottom")])],"isStart":false});
            fillet(context, id + "F15", {"entities" : qUnion([Q0]), "radius" : 2 * mm, "tangentPropagation" : true, "allowEdgeOverflow" : false});
        }
        {
            var Q0;
            {var subQ0=sQuery(id+"F0.wireOp",EDGE,"E21.filletArc");var subQ1=sQuery(id+"F0.wireOp",EDGE,"E7");var subQ2=sQuery(id+"F0.wireOp",EDGE,"E6");var subQ3=sQuery(id+"F0.wireOp",EDGE,"E5");var subQ4=sQuery(id+"F0.wireOp",EDGE,"E4");var subQ5=sQuery(id+"F0.wireOp",EDGE,"E22.filletArc");var subQ6=sQuery(id+"F0.wireOp",EDGE,"E1.bottom");var subQ7=sQuery(id+"F0.wireOp",EDGE,"E1.right");var subQ8=sQuery(id+"F0.wireOp",EDGE,"E1.top");var subQ9=sQuery(id+"F0.wireOp",EDGE,"E1.left");var subQ10=sQuery(id+"F0.wireOp",EDGE,"E23.filletArc");var subQ11=sQuery(id+"F0.wireOp",EDGE,"E24.filletArc");Q0=makeQuery(id+"F2.boolean.opBoolean","SPLIT",FACE,{"disambiguationData":[TD([makeQuery(id+"F1.opExtrude","SWEPT_FACE",FACE,{"disambiguationData":[OSD([subQ6])]})])],"derivedFrom":makeQuery(id+"F1.opExtrude","CAP_FACE",FACE,{"disambiguationData":[OSD([subQ6,subQ8,subQ9,subQ7,subQ4,subQ3,subQ2,subQ1,subQ0,subQ5,subQ10,subQ11])],"isStart":true})});}
            var sketch = newSketch(context, id + "F16", { "sketchPlane" : qUnion([Q0])});
            skLineSegment(sketch, "E79.0", {"start": v(-80, -80) * mm, "end": v(-80, 80) * mm});
            skLineSegment(sketch, "E79.1", {"start": v(-70, 90) * mm, "end": v(70, 90) * mm});
            skLineSegment(sketch, "E79.2", {"start": v(80, -80) * mm, "end": v(80, 80) * mm});
            skLineSegment(sketch, "E79.3", {"start": v(-70, -90) * mm, "end": v(70, -90) * mm});
            skArc(sketch, "E79.4", {"start": v(70, -90) * mm, "mid": v(77.07, -87.07) * mm, "end": v(80, -80) * mm});
            skArc(sketch, "E79.5", {"start": v(80, 80) * mm, "mid": v(77.07, 87.07) * mm, "end": v(70, 90) * mm});
            skArc(sketch, "E79.6", {"start": v(-70, 90) * mm, "mid": v(-77.07, 87.07) * mm, "end": v(-80, 80) * mm});
            skArc(sketch, "E79.7", {"start": v(-80, -80) * mm, "mid": v(-77.07, -87.07) * mm, "end": v(-70, -90) * mm});
            skArc(sketch, "E79.8", {"start": v(-56.15, -48.18) * mm, "mid": v(0, -67.5) * mm, "end": v(56.15, -48.18) * mm});
            skLineSegment(sketch, "E79.9", {"start": v(-60, 40.3) * mm, "end": v(-60, -40.3) * mm});
            skArc(sketch, "E79.10", {"start": v(56.15, 48.18) * mm, "mid": v(0, 67.5) * mm, "end": v(-56.15, 48.18) * mm});
            skLineSegment(sketch, "E79.11", {"start": v(60, 40.3) * mm, "end": v(60, -40.3) * mm});
            skArc(sketch, "E79.12", {"start": v(56.15, -48.18) * mm, "mid": v(58.99, -44.68) * mm, "end": v(60, -40.3) * mm});
            skArc(sketch, "E79.13", {"start": v(60, 40.3) * mm, "mid": v(58.99, 44.68) * mm, "end": v(56.15, 48.18) * mm});
            skCircle(sketch, "E79.14", {"center": v(-60, -67.5) * mm, "radius": 4 * mm});
            skCircle(sketch, "E79.15", {"center": v(60, -67.5) * mm, "radius": 4 * mm});
            skCircle(sketch, "E79.16", {"center": v(60, 67.5) * mm, "radius": 4 * mm});
            skCircle(sketch, "E79.17", {"center": v(-60, 67.5) * mm, "radius": 4 * mm});
            skArc(sketch, "E79.18", {"start": v(-60, -40.3) * mm, "mid": v(-58.99, -44.68) * mm, "end": v(-56.15, -48.18) * mm});
            skArc(sketch, "E79.19", {"start": v(-56.15, 48.18) * mm, "mid": v(-58.99, 44.68) * mm, "end": v(-60, 40.3) * mm});
            skLineSegment(sketch, "E80", {"start": v(-33, 90) * mm, "end": v(-15, 108) * mm});
            skLineSegment(sketch, "E81", {"start": v(33, 90) * mm, "end": v(15, 108) * mm});
            skLineSegment(sketch, "E82", {"start": v(-15, 108) * mm, "end": v(-15, 120) * mm});
            skLineSegment(sketch, "E83", {"start": v(15, 108) * mm, "end": v(15, 120) * mm});
            skArc(sketch, "E84", {"start": v(15, 120) * mm, "mid": v(0, 135) * mm, "end": v(-15, 120) * mm});
            skCircle(sketch, "E85", {"center": v(0, 120) * mm, "radius": 6 * mm});
            skLineSegment(sketch, "E86", {"start": v(0, 120) * mm, "end": v(0, 90) * mm, "construction": true});
            skLineSegment(sketch, "E87", {"start": v(-80, 0) * mm, "end": v(80, 0) * mm, "construction": true});
            skLineSegment(sketch, "E88.MirrorCS", {"start": v(-15, -108) * mm, "end": v(-15, -120) * mm});
            skLineSegment(sketch, "E89.MirrorCS", {"start": v(15, -108) * mm, "end": v(15, -120) * mm});
            skLineSegment(sketch, "E90.MirrorCS", {"start": v(-33, -90) * mm, "end": v(-15, -108) * mm});
            skLineSegment(sketch, "E91.MirrorCS", {"start": v(0, -120) * mm, "end": v(0, -90) * mm, "construction": true});
            skCircle(sketch, "E92.MirrorC", {"center": v(0, -120) * mm, "radius": 6 * mm});
            skArc(sketch, "E93.MirrorCS", {"start": v(15, -120) * mm, "mid": v(0, -135) * mm, "end": v(-15, -120) * mm});
            skLineSegment(sketch, "E94.MirrorCS", {"start": v(33, -90) * mm, "end": v(15, -108) * mm});
            skSolve(sketch);
        }
        {
            var Q0;
            Q0 = qSketchRegion(id + "F16", true);
            var Q1;
            Q1=makeQuery(id+"F2.opExtrude","CAP_FACE",FACE,{"disambiguationData":[OSD([sQuery(id+"F0.wireOp",EDGE,"E12"),sQuery(id+"F0.wireOp",EDGE,"E13"),sQuery(id+"F0.wireOp",EDGE,"E14"),sQuery(id+"F0.wireOp",EDGE,"E15"),sQuery(id+"F0.wireOp",EDGE,"E17.filletArc"),sQuery(id+"F0.wireOp",EDGE,"E18.filletArc"),sQuery(id+"F0.wireOp",EDGE,"E19.filletArc"),sQuery(id+"F0.wireOp",EDGE,"E20.filletArc"),sQuery(id+"F0.wireOp",EDGE,"E25.0"),sQuery(id+"F0.wireOp",EDGE,"E25.1"),sQuery(id+"F0.wireOp",EDGE,"E25.2"),sQuery(id+"F0.wireOp",EDGE,"E25.3"),sQuery(id+"F0.wireOp",EDGE,"E25.4"),sQuery(id+"F0.wireOp",EDGE,"E25.5"),sQuery(id+"F0.wireOp",EDGE,"E25.6"),sQuery(id+"F0.wireOp",EDGE,"E25.7")])],"isStart":false});
            extrude(context, id + "F17", {"entities" : qUnion([Q0]), "endBound" : BoundingType.UP_TO_SURFACE, "endBoundEntityFace" : qUnion([Q1]), "depth" : 25 * mm});
        }
    });
